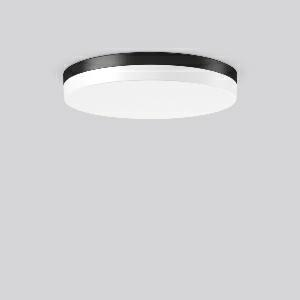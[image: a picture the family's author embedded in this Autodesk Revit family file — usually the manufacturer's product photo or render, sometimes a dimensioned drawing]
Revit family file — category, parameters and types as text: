
# Revit family: flat_slim_round_312634_0031_1_730_f22d
name_source: partatom
category: Lighting Fixtures
units: mm (PartAtom-declared; Revit-internal decimal feet)

## family parameters
Cut with Voids When Loaded = No
Host = Face
Light Source = No
Part Type = Normal
Room Calculation Point = No
Round Connector Dimension = Use Diameter
Shared = No

## types (1)
- MultiLumen 1 830 (1 x LED Modul 830, 3500 lm, 3000)
    Apparent Load = 24 VA
    CIE Flux Codes = 38 68 89 85 100
    Color Rendering = 80
    Color Temperature = 3000
    Default Elevation = 1800 mm
    Height = 70 mm
    Lamp = 1 x LED Modul 830
    Lamp Light Flux = 3500 lm
    Lamp count = 1
    Length = 480 mm
    Lifetime = 50000 h
    Luminous efficacy = 146 lm/W
    Manufacturer = RZB
    ModVariant = No
    Model = 312634.0031.1.730
    Mounting Place = Ceiling
    Mounting Type = Surface mounted
    Number of Poles = 1
    OnlyDefault = Yes
    Power Factor = 1
    Product Name = FLAT SLIM round
    Product group = Surface mounted ceiling and wall luminaires
    ProductGroupID = 305
    Protection Class = Protection class I
    Protection Degree = Degree of protection
    RLX_Detail_Level = 1
    RLX_Emergency_Light_Flux = 0 lm
    RLX_Emergency_Type = 0
    RLX_Emergency_Type_DB = No
    RlxData = <blob elided: 23305 chars, md5=0b958482>
    Socket = socket
    Standby Power = 0 W
    System Light Flux = 3500 lm
    System Power = 24 W
    Type Comments = MultiLumen 1 830
    Type Image = 312633.0031.jpg
    URL = http://relux.com
    VarID = multilumen_1_830
    Voltage = 0 V
    Weight = 0.00 kg
    Width = 0 mm  [stored 0 ft]

note: [stored X ft] marks values corroborated as IEEE doubles in the binary element streams (Revit-internal decimal feet)

## geometry (parser evidence)
native form markers: Blend x4, Sweep x13
no freeform markers — native parametric forms only
